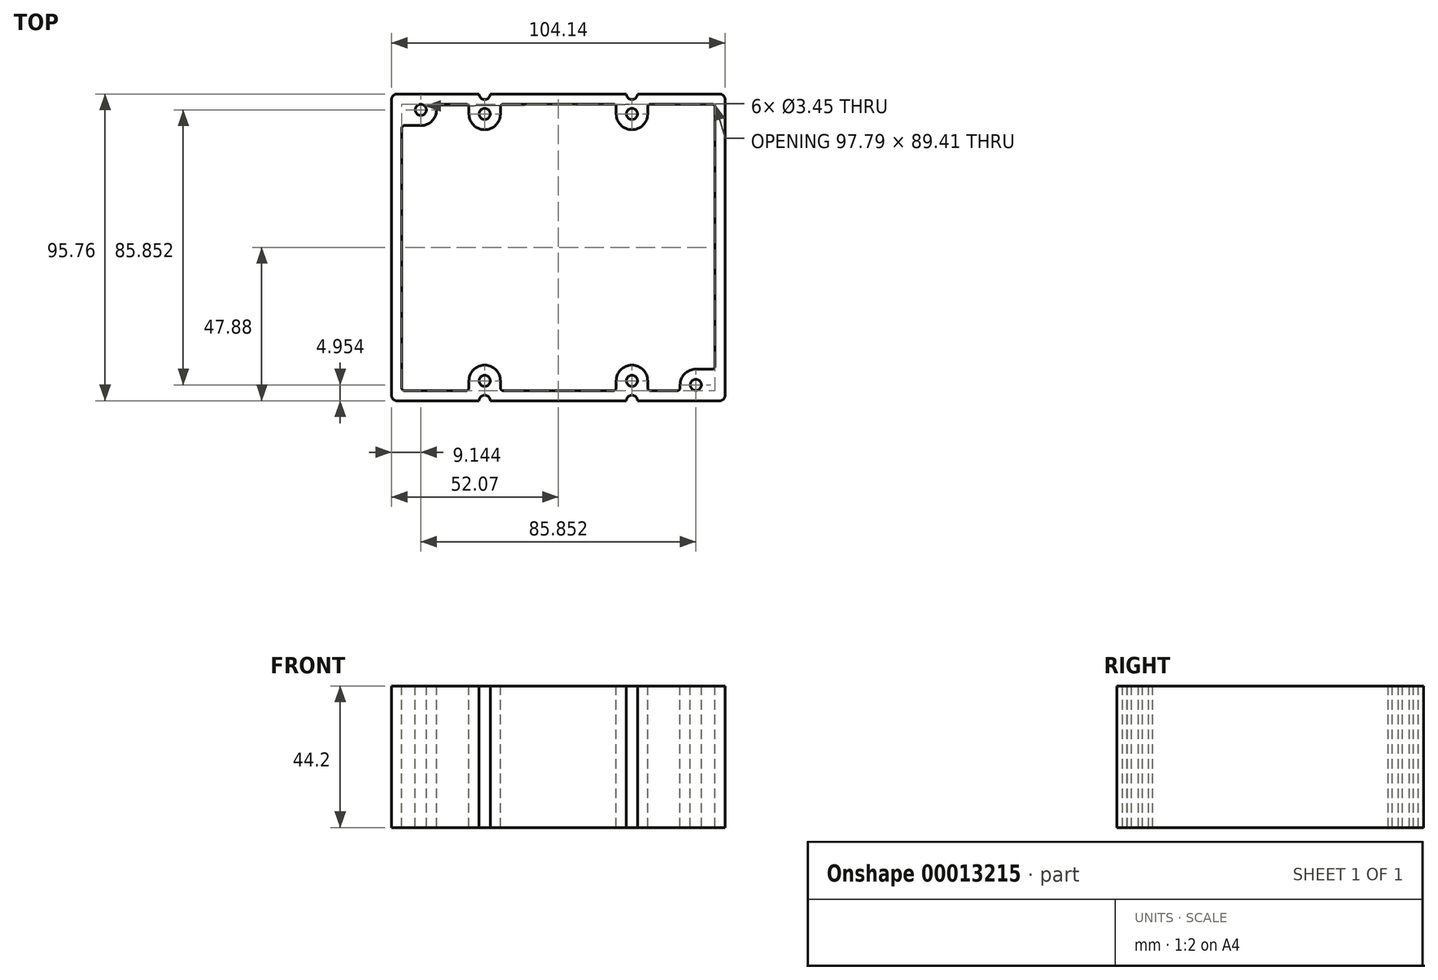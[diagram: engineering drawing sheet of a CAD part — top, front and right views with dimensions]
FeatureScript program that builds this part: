
annotation { "Feature Type Name" : "Feature", "Feature Type Description" : "" }
export const myFeature = defineFeature(function(context is Context, id is Id, definition is map)
    precondition{}
    {
        {
            var Q0;
            Q0=qCreatedBy(makeId("Front.planeOp"),FACE);
            var sketch = newSketch(context, id + "F0", { "sketchPlane" : qUnion([Q0])});
            skLineSegment(sketch, "E0.bottom", {"start": v(1.73, 0) * mm, "end": v(27.36, 0) * mm});
            skLineSegment(sketch, "E0.top", {"start": v(1.73, 95.76) * mm, "end": v(27.36, 95.76) * mm});
            skLineSegment(sketch, "E0.left", {"start": v(0, 1.73) * mm, "end": v(0, 94.03) * mm});
            skLineSegment(sketch, "E0.right", {"start": v(104.14, 1.73) * mm, "end": v(104.14, 94.03) * mm});
            skLineSegment(sketch, "E1", {"start": v(0, 47.88) * mm, "end": v(104.14, 47.88) * mm, "construction": true});
            skLineSegment(sketch, "E2", {"start": v(52.07, 95.76) * mm, "end": v(52.07, 0) * mm, "construction": true});
            skCircle(sketch, "E3", {"center": v(29.08, 89.53) * mm, "radius": 1.73 * mm});
            skCircle(sketch, "E4", {"center": v(29.08, 6.22) * mm, "radius": 1.73 * mm});
            skCircle(sketch, "E5", {"center": v(75.06, 89.53) * mm, "radius": 1.73 * mm});
            skCircle(sketch, "E6", {"center": v(75.06, 6.22) * mm, "radius": 1.73 * mm});
            skLineSegment(sketch, "E7", {"start": v(29.08, 89.53) * mm, "end": v(29.08, 6.22) * mm, "construction": true});
            skLineSegment(sketch, "E8", {"start": v(75.06, 6.22) * mm, "end": v(75.06, 89.53) * mm, "construction": true});
            skLineSegment(sketch, "E9", {"start": v(29.08, 89.53) * mm, "end": v(75.06, 89.53) * mm, "construction": true});
            skLineSegment(sketch, "E10", {"start": v(75.06, 6.22) * mm, "end": v(29.08, 6.22) * mm, "construction": true});
            skCircle(sketch, "E11", {"center": v(9.14, 4.95) * mm, "radius": 1.73 * mm});
            skCircle(sketch, "E12", {"center": v(95, 90.8) * mm, "radius": 1.73 * mm});
            skLineSegment(sketch, "E13.bottom", {"start": v(9.14, 4.95) * mm, "end": v(95, 4.95) * mm, "construction": true});
            skLineSegment(sketch, "E13.top", {"start": v(9.14, 90.8) * mm, "end": v(95, 90.8) * mm, "construction": true});
            skLineSegment(sketch, "E13.left", {"start": v(9.14, 4.95) * mm, "end": v(9.14, 90.8) * mm, "construction": true});
            skLineSegment(sketch, "E13.right", {"start": v(95, 4.95) * mm, "end": v(95, 90.8) * mm, "construction": true});
            skArc(sketch, "E14", {"start": v(27.36, 95.76) * mm, "mid": v(29.08, 94.03) * mm, "end": v(30.81, 95.76) * mm});
            skArc(sketch, "E15.0.MirrorCS", {"start": v(76.78, 95.76) * mm, "mid": v(75.06, 94.03) * mm, "end": v(73.33, 95.76) * mm});
            skArc(sketch, "E16.0.MirrorCS", {"start": v(27.36, 0) * mm, "mid": v(29.08, 1.73) * mm, "end": v(30.81, 0) * mm});
            skArc(sketch, "E17.0.MirrorCS", {"start": v(76.78, 0) * mm, "mid": v(75.06, 1.73) * mm, "end": v(73.33, 0) * mm});
            skPoint(sketch, "E18.visualSharp", {"position": v(0, 95.76) * mm});
            skArc(sketch, "E18.filletArc", {"start": v(1.73, 95.76) * mm, "mid": v(0.5, 95.25) * mm, "end": v(0, 94.03) * mm});
            skPoint(sketch, "E19.visualSharp", {"position": v(0, 0) * mm});
            skArc(sketch, "E19.filletArc", {"start": v(0, 1.73) * mm, "mid": v(0.5, 0.5) * mm, "end": v(1.73, 0) * mm});
            skPoint(sketch, "E20.visualSharp", {"position": v(104.14, 0) * mm});
            skArc(sketch, "E20.filletArc", {"start": v(102.41, 0) * mm, "mid": v(103.63, 0.5) * mm, "end": v(104.14, 1.73) * mm});
            skPoint(sketch, "E21.visualSharp", {"position": v(104.14, 95.76) * mm});
            skArc(sketch, "E21.filletArc", {"start": v(104.14, 94.03) * mm, "mid": v(103.63, 95.25) * mm, "end": v(102.41, 95.76) * mm});
            skLineSegment(sketch, "E22.trimOffspring", {"start": v(30.81, 95.76) * mm, "end": v(73.33, 95.76) * mm});
            skLineSegment(sketch, "E23.trimOffspring", {"start": v(76.78, 95.76) * mm, "end": v(102.41, 95.76) * mm});
            skLineSegment(sketch, "E24.trimOffspring", {"start": v(30.81, 0) * mm, "end": v(73.33, 0) * mm});
            skLineSegment(sketch, "E25.trimOffspring", {"start": v(76.78, 0) * mm, "end": v(102.41, 0) * mm});
            skLineSegment(sketch, "E26.0", {"start": v(80.82, 3.18) * mm, "end": v(100.1, 3.18) * mm});
            skLineSegment(sketch, "E26.5", {"start": v(100.97, 4.04) * mm, "end": v(100.97, 85.04) * mm});
            skLineSegment(sketch, "E26.6", {"start": v(3.17, 10.72) * mm, "end": v(3.17, 91.72) * mm});
            skLineSegment(sketch, "E26.7", {"start": v(4.04, 92.58) * mm, "end": v(23.32, 92.58) * mm});
            skLineSegment(sketch, "E26.9", {"start": v(34.85, 92.58) * mm, "end": v(69.3, 92.58) * mm});
            skLineSegment(sketch, "E26.11", {"start": v(80.82, 92.58) * mm, "end": v(89.23, 92.58) * mm});
            skArc(sketch, "E27.0", {"start": v(24.18, 89.53) * mm, "mid": v(29.08, 84.63) * mm, "end": v(33.99, 89.53) * mm});
            skArc(sketch, "E28.0", {"start": v(70.15, 89.53) * mm, "mid": v(75.06, 84.63) * mm, "end": v(79.96, 89.53) * mm});
            skLineSegment(sketch, "E29.0", {"start": v(71.22, 3.18) * mm, "end": v(71.22, 3.18) * mm});
            skArc(sketch, "E30.0", {"start": v(90.1, 90.8) * mm, "mid": v(91.53, 87.34) * mm, "end": v(95, 85.9) * mm});
            skArc(sketch, "E31.0", {"start": v(33.99, 6.22) * mm, "mid": v(29.08, 11.13) * mm, "end": v(24.18, 6.22) * mm});
            skArc(sketch, "E32.0", {"start": v(14.05, 4.95) * mm, "mid": v(12.61, 8.42) * mm, "end": v(9.14, 9.86) * mm});
            skLineSegment(sketch, "E33", {"start": v(95, 85.9) * mm, "end": v(100.1, 85.9) * mm});
            skLineSegment(sketch, "E34", {"start": v(90.1, 90.8) * mm, "end": v(90.1, 91.72) * mm});
            skLineSegment(sketch, "E35", {"start": v(79.96, 89.53) * mm, "end": v(79.96, 91.72) * mm});
            skLineSegment(sketch, "E36", {"start": v(70.15, 89.53) * mm, "end": v(70.15, 91.72) * mm});
            skLineSegment(sketch, "E37", {"start": v(33.99, 89.53) * mm, "end": v(33.99, 91.72) * mm});
            skLineSegment(sketch, "E38", {"start": v(24.18, 89.53) * mm, "end": v(24.18, 91.72) * mm});
            skLineSegment(sketch, "E39", {"start": v(9.14, 9.86) * mm, "end": v(4.04, 9.86) * mm});
            skLineSegment(sketch, "E40", {"start": v(14.05, 4.95) * mm, "end": v(14.05, 4.04) * mm});
            skLineSegment(sketch, "E41", {"start": v(24.18, 6.22) * mm, "end": v(24.18, 4.04) * mm});
            skLineSegment(sketch, "E42", {"start": v(33.99, 6.22) * mm, "end": v(33.99, 4.04) * mm});
            skLineSegment(sketch, "E43", {"start": v(79.96, 6.22) * mm, "end": v(79.96, 4.04) * mm});
            skLineSegment(sketch, "E44", {"start": v(70.15, 6.22) * mm, "end": v(70.15, 4.04) * mm});
            skArc(sketch, "E45.trimOffspring", {"start": v(79.96, 6.22) * mm, "mid": v(75.06, 11.13) * mm, "end": v(70.15, 6.22) * mm});
            skLineSegment(sketch, "E46.trimOffspring", {"start": v(34.85, 3.18) * mm, "end": v(69.3, 3.18) * mm});
            skLineSegment(sketch, "E47.trimOffspring", {"start": v(14.9, 3.18) * mm, "end": v(23.32, 3.18) * mm});
            skPoint(sketch, "E48.visualSharp", {"position": v(3.17, 92.58) * mm});
            skArc(sketch, "E48.filletArc", {"start": v(4.04, 92.58) * mm, "mid": v(3.43, 92.33) * mm, "end": v(3.18, 91.72) * mm});
            skPoint(sketch, "E49.visualSharp", {"position": v(24.18, 92.58) * mm});
            skArc(sketch, "E49.filletArc", {"start": v(24.18, 91.72) * mm, "mid": v(23.93, 92.33) * mm, "end": v(23.32, 92.58) * mm});
            skPoint(sketch, "E50.visualSharp", {"position": v(33.99, 92.58) * mm});
            skArc(sketch, "E50.filletArc", {"start": v(34.85, 92.58) * mm, "mid": v(34.24, 92.33) * mm, "end": v(33.99, 91.72) * mm});
            skPoint(sketch, "E51.visualSharp", {"position": v(70.15, 92.58) * mm});
            skArc(sketch, "E51.filletArc", {"start": v(70.15, 91.72) * mm, "mid": v(69.9, 92.33) * mm, "end": v(69.3, 92.58) * mm});
            skPoint(sketch, "E52.visualSharp", {"position": v(79.96, 92.58) * mm});
            skArc(sketch, "E52.filletArc", {"start": v(80.82, 92.58) * mm, "mid": v(80.21, 92.33) * mm, "end": v(79.96, 91.72) * mm});
            skPoint(sketch, "E53.visualSharp", {"position": v(90.1, 92.58) * mm});
            skArc(sketch, "E53.filletArc", {"start": v(90.1, 91.72) * mm, "mid": v(89.84, 92.33) * mm, "end": v(89.23, 92.58) * mm});
            skPoint(sketch, "E54.visualSharp", {"position": v(100.97, 85.9) * mm});
            skArc(sketch, "E54.filletArc", {"start": v(100.97, 85.04) * mm, "mid": v(100.71, 85.65) * mm, "end": v(100.1, 85.9) * mm});
            skPoint(sketch, "E55.visualSharp", {"position": v(100.97, 3.18) * mm});
            skArc(sketch, "E55.filletArc", {"start": v(100.1, 3.17) * mm, "mid": v(100.71, 3.43) * mm, "end": v(100.97, 4.04) * mm});
            skPoint(sketch, "E56.visualSharp", {"position": v(79.96, 3.18) * mm});
            skArc(sketch, "E56.filletArc", {"start": v(79.96, 4.04) * mm, "mid": v(80.21, 3.43) * mm, "end": v(80.82, 3.18) * mm});
            skPoint(sketch, "E57.visualSharp", {"position": v(70.15, 3.18) * mm});
            skArc(sketch, "E57.filletArc", {"start": v(69.3, 3.18) * mm, "mid": v(69.9, 3.43) * mm, "end": v(70.15, 4.04) * mm});
            skPoint(sketch, "E58.visualSharp", {"position": v(33.99, 3.18) * mm});
            skArc(sketch, "E58.filletArc", {"start": v(33.99, 4.04) * mm, "mid": v(34.24, 3.43) * mm, "end": v(34.85, 3.18) * mm});
            skPoint(sketch, "E59.visualSharp", {"position": v(24.18, 3.18) * mm});
            skArc(sketch, "E59.filletArc", {"start": v(23.32, 3.18) * mm, "mid": v(23.93, 3.43) * mm, "end": v(24.18, 4.04) * mm});
            skPoint(sketch, "E60.visualSharp", {"position": v(14.05, 3.18) * mm});
            skArc(sketch, "E60.filletArc", {"start": v(14.05, 4.04) * mm, "mid": v(14.3, 3.43) * mm, "end": v(14.9, 3.18) * mm});
            skPoint(sketch, "E61.visualSharp", {"position": v(3.17, 9.86) * mm});
            skArc(sketch, "E61.filletArc", {"start": v(3.17, 10.72) * mm, "mid": v(3.43, 10.1) * mm, "end": v(4.04, 9.86) * mm});
            skSolve(sketch);
        }
        {
            var Q0;
            Q0 = qSketchRegion(id + "F0", true);
            extrude(context, id + "F1", {"entities" : qUnion([Q0]), "depth" : 44.2 * mm});
        }
        {
            var Q0;
            Q0=makeQuery(id+"F1.opExtrude","SWEPT_BODY",BODY,{"disambiguationData":[OSD([sQuery(id+"F0.wireOp",EDGE,"E0.bottom"),sQuery(id+"F0.wireOp",EDGE,"E0.top"),sQuery(id+"F0.wireOp",EDGE,"E0.left"),sQuery(id+"F0.wireOp",EDGE,"E0.right"),sQuery(id+"F0.wireOp",EDGE,"E3"),sQuery(id+"F0.wireOp",EDGE,"E4"),sQuery(id+"F0.wireOp",EDGE,"E5"),sQuery(id+"F0.wireOp",EDGE,"E6"),sQuery(id+"F0.wireOp",EDGE,"E11"),sQuery(id+"F0.wireOp",EDGE,"E12"),sQuery(id+"F0.wireOp",EDGE,"E14"),sQuery(id+"F0.wireOp",EDGE,"E15.0.MirrorCS"),sQuery(id+"F0.wireOp",EDGE,"E16.0.MirrorCS"),sQuery(id+"F0.wireOp",EDGE,"E17.0.MirrorCS"),sQuery(id+"F0.wireOp",EDGE,"E18.filletArc"),sQuery(id+"F0.wireOp",EDGE,"E19.filletArc"),sQuery(id+"F0.wireOp",EDGE,"E20.filletArc"),sQuery(id+"F0.wireOp",EDGE,"E21.filletArc"),sQuery(id+"F0.wireOp",EDGE,"E22.trimOffspring"),sQuery(id+"F0.wireOp",EDGE,"E23.trimOffspring"),sQuery(id+"F0.wireOp",EDGE,"E24.trimOffspring"),sQuery(id+"F0.wireOp",EDGE,"E25.trimOffspring"),sQuery(id+"F0.wireOp",EDGE,"E26.0"),sQuery(id+"F0.wireOp",EDGE,"E26.5"),sQuery(id+"F0.wireOp",EDGE,"E26.6"),sQuery(id+"F0.wireOp",EDGE,"E26.7"),sQuery(id+"F0.wireOp",EDGE,"E26.9"),sQuery(id+"F0.wireOp",EDGE,"E26.11"),sQuery(id+"F0.wireOp",EDGE,"E27.0"),sQuery(id+"F0.wireOp",EDGE,"E28.0"),sQuery(id+"F0.wireOp",EDGE,"E30.0"),sQuery(id+"F0.wireOp",EDGE,"E31.0"),sQuery(id+"F0.wireOp",EDGE,"E32.0"),sQuery(id+"F0.wireOp",EDGE,"E33"),sQuery(id+"F0.wireOp",EDGE,"E34"),sQuery(id+"F0.wireOp",EDGE,"E35"),sQuery(id+"F0.wireOp",EDGE,"E36"),sQuery(id+"F0.wireOp",EDGE,"E37"),sQuery(id+"F0.wireOp",EDGE,"E38"),sQuery(id+"F0.wireOp",EDGE,"E39"),sQuery(id+"F0.wireOp",EDGE,"E40"),sQuery(id+"F0.wireOp",EDGE,"E41"),sQuery(id+"F0.wireOp",EDGE,"E42"),sQuery(id+"F0.wireOp",EDGE,"E43"),sQuery(id+"F0.wireOp",EDGE,"E44"),sQuery(id+"F0.wireOp",EDGE,"E45.trimOffspring"),sQuery(id+"F0.wireOp",EDGE,"E46.trimOffspring"),sQuery(id+"F0.wireOp",EDGE,"E47.trimOffspring"),sQuery(id+"F0.wireOp",EDGE,"E48.filletArc"),sQuery(id+"F0.wireOp",EDGE,"E49.filletArc"),sQuery(id+"F0.wireOp",EDGE,"E50.filletArc"),sQuery(id+"F0.wireOp",EDGE,"E51.filletArc"),sQuery(id+"F0.wireOp",EDGE,"E52.filletArc"),sQuery(id+"F0.wireOp",EDGE,"E53.filletArc"),sQuery(id+"F0.wireOp",EDGE,"E54.filletArc"),sQuery(id+"F0.wireOp",EDGE,"E55.filletArc"),sQuery(id+"F0.wireOp",EDGE,"E56.filletArc"),sQuery(id+"F0.wireOp",EDGE,"E57.filletArc"),sQuery(id+"F0.wireOp",EDGE,"E58.filletArc"),sQuery(id+"F0.wireOp",EDGE,"E59.filletArc"),sQuery(id+"F0.wireOp",EDGE,"E60.filletArc"),sQuery(id+"F0.wireOp",EDGE,"E61.filletArc")])]});
            transform(context, id + "F2", {"entities" : qUnion([Q0]), "transformType" : TransformType.TRANSLATION_3D, "dx" : -52.07 * mm, "dy" : 44.2 * mm, "dz" : -47.88 * mm, "makeCopy" : false});
        }
        {
            var Q0;
            Q0=qCreatedBy(makeId("Front.planeOp"),FACE);
            var sketch = newSketch(context, id + "F3", { "sketchPlane" : qUnion([Q0])});
            skLineSegment(sketch, "E62", {"start": v(-48.55, 0) * mm, "end": v(0, 0) * mm});
            skSolve(sketch);
        }
        {
            var Q0;
            Q0=makeQuery(id+"F1.opExtrude","SWEPT_BODY",BODY,{"disambiguationData":[OSD([sQuery(id+"F0.wireOp",EDGE,"E0.bottom"),sQuery(id+"F0.wireOp",EDGE,"E0.top"),sQuery(id+"F0.wireOp",EDGE,"E0.left"),sQuery(id+"F0.wireOp",EDGE,"E0.right"),sQuery(id+"F0.wireOp",EDGE,"E3"),sQuery(id+"F0.wireOp",EDGE,"E4"),sQuery(id+"F0.wireOp",EDGE,"E5"),sQuery(id+"F0.wireOp",EDGE,"E6"),sQuery(id+"F0.wireOp",EDGE,"E11"),sQuery(id+"F0.wireOp",EDGE,"E12"),sQuery(id+"F0.wireOp",EDGE,"E14"),sQuery(id+"F0.wireOp",EDGE,"E15.0.MirrorCS"),sQuery(id+"F0.wireOp",EDGE,"E16.0.MirrorCS"),sQuery(id+"F0.wireOp",EDGE,"E17.0.MirrorCS"),sQuery(id+"F0.wireOp",EDGE,"E18.filletArc"),sQuery(id+"F0.wireOp",EDGE,"E19.filletArc"),sQuery(id+"F0.wireOp",EDGE,"E20.filletArc"),sQuery(id+"F0.wireOp",EDGE,"E21.filletArc"),sQuery(id+"F0.wireOp",EDGE,"E22.trimOffspring"),sQuery(id+"F0.wireOp",EDGE,"E23.trimOffspring"),sQuery(id+"F0.wireOp",EDGE,"E24.trimOffspring"),sQuery(id+"F0.wireOp",EDGE,"E25.trimOffspring"),sQuery(id+"F0.wireOp",EDGE,"E26.0"),sQuery(id+"F0.wireOp",EDGE,"E26.5"),sQuery(id+"F0.wireOp",EDGE,"E26.6"),sQuery(id+"F0.wireOp",EDGE,"E26.7"),sQuery(id+"F0.wireOp",EDGE,"E26.9"),sQuery(id+"F0.wireOp",EDGE,"E26.11"),sQuery(id+"F0.wireOp",EDGE,"E27.0"),sQuery(id+"F0.wireOp",EDGE,"E28.0"),sQuery(id+"F0.wireOp",EDGE,"E30.0"),sQuery(id+"F0.wireOp",EDGE,"E31.0"),sQuery(id+"F0.wireOp",EDGE,"E32.0"),sQuery(id+"F0.wireOp",EDGE,"E33"),sQuery(id+"F0.wireOp",EDGE,"E34"),sQuery(id+"F0.wireOp",EDGE,"E35"),sQuery(id+"F0.wireOp",EDGE,"E36"),sQuery(id+"F0.wireOp",EDGE,"E37"),sQuery(id+"F0.wireOp",EDGE,"E38"),sQuery(id+"F0.wireOp",EDGE,"E39"),sQuery(id+"F0.wireOp",EDGE,"E40"),sQuery(id+"F0.wireOp",EDGE,"E41"),sQuery(id+"F0.wireOp",EDGE,"E42"),sQuery(id+"F0.wireOp",EDGE,"E43"),sQuery(id+"F0.wireOp",EDGE,"E44"),sQuery(id+"F0.wireOp",EDGE,"E45.trimOffspring"),sQuery(id+"F0.wireOp",EDGE,"E46.trimOffspring"),sQuery(id+"F0.wireOp",EDGE,"E47.trimOffspring"),sQuery(id+"F0.wireOp",EDGE,"E48.filletArc"),sQuery(id+"F0.wireOp",EDGE,"E49.filletArc"),sQuery(id+"F0.wireOp",EDGE,"E50.filletArc"),sQuery(id+"F0.wireOp",EDGE,"E51.filletArc"),sQuery(id+"F0.wireOp",EDGE,"E52.filletArc"),sQuery(id+"F0.wireOp",EDGE,"E53.filletArc"),sQuery(id+"F0.wireOp",EDGE,"E54.filletArc"),sQuery(id+"F0.wireOp",EDGE,"E55.filletArc"),sQuery(id+"F0.wireOp",EDGE,"E56.filletArc"),sQuery(id+"F0.wireOp",EDGE,"E57.filletArc"),sQuery(id+"F0.wireOp",EDGE,"E58.filletArc"),sQuery(id+"F0.wireOp",EDGE,"E59.filletArc"),sQuery(id+"F0.wireOp",EDGE,"E60.filletArc"),sQuery(id+"F0.wireOp",EDGE,"E61.filletArc")])]});
            var Q1;
            Q1=sQuery(id+"F3.wireOp",EDGE,"E62");
            transform(context, id + "F4", {"entities" : qUnion([Q0]), "transformType" : TransformType.ROTATION, "transformAxis" : qUnion([Q1]), "angle" : 90 * degree, "makeCopy" : false});
        }
        {
            var Q0;
            Q0=makeQuery(id+"F1.opExtrude","SWEPT_BODY",BODY,{"disambiguationData":[OSD([sQuery(id+"F0.wireOp",EDGE,"E0.bottom"),sQuery(id+"F0.wireOp",EDGE,"E0.top"),sQuery(id+"F0.wireOp",EDGE,"E0.left"),sQuery(id+"F0.wireOp",EDGE,"E0.right"),sQuery(id+"F0.wireOp",EDGE,"E3"),sQuery(id+"F0.wireOp",EDGE,"E4"),sQuery(id+"F0.wireOp",EDGE,"E5"),sQuery(id+"F0.wireOp",EDGE,"E6"),sQuery(id+"F0.wireOp",EDGE,"E11"),sQuery(id+"F0.wireOp",EDGE,"E12"),sQuery(id+"F0.wireOp",EDGE,"E14"),sQuery(id+"F0.wireOp",EDGE,"E15.0.MirrorCS"),sQuery(id+"F0.wireOp",EDGE,"E16.0.MirrorCS"),sQuery(id+"F0.wireOp",EDGE,"E17.0.MirrorCS"),sQuery(id+"F0.wireOp",EDGE,"E18.filletArc"),sQuery(id+"F0.wireOp",EDGE,"E19.filletArc"),sQuery(id+"F0.wireOp",EDGE,"E20.filletArc"),sQuery(id+"F0.wireOp",EDGE,"E21.filletArc"),sQuery(id+"F0.wireOp",EDGE,"E22.trimOffspring"),sQuery(id+"F0.wireOp",EDGE,"E23.trimOffspring"),sQuery(id+"F0.wireOp",EDGE,"E24.trimOffspring"),sQuery(id+"F0.wireOp",EDGE,"E25.trimOffspring"),sQuery(id+"F0.wireOp",EDGE,"E26.0"),sQuery(id+"F0.wireOp",EDGE,"E26.5"),sQuery(id+"F0.wireOp",EDGE,"E26.6"),sQuery(id+"F0.wireOp",EDGE,"E26.7"),sQuery(id+"F0.wireOp",EDGE,"E26.9"),sQuery(id+"F0.wireOp",EDGE,"E26.11"),sQuery(id+"F0.wireOp",EDGE,"E27.0"),sQuery(id+"F0.wireOp",EDGE,"E28.0"),sQuery(id+"F0.wireOp",EDGE,"E30.0"),sQuery(id+"F0.wireOp",EDGE,"E31.0"),sQuery(id+"F0.wireOp",EDGE,"E32.0"),sQuery(id+"F0.wireOp",EDGE,"E33"),sQuery(id+"F0.wireOp",EDGE,"E34"),sQuery(id+"F0.wireOp",EDGE,"E35"),sQuery(id+"F0.wireOp",EDGE,"E36"),sQuery(id+"F0.wireOp",EDGE,"E37"),sQuery(id+"F0.wireOp",EDGE,"E38"),sQuery(id+"F0.wireOp",EDGE,"E39"),sQuery(id+"F0.wireOp",EDGE,"E40"),sQuery(id+"F0.wireOp",EDGE,"E41"),sQuery(id+"F0.wireOp",EDGE,"E42"),sQuery(id+"F0.wireOp",EDGE,"E43"),sQuery(id+"F0.wireOp",EDGE,"E44"),sQuery(id+"F0.wireOp",EDGE,"E45.trimOffspring"),sQuery(id+"F0.wireOp",EDGE,"E46.trimOffspring"),sQuery(id+"F0.wireOp",EDGE,"E47.trimOffspring"),sQuery(id+"F0.wireOp",EDGE,"E48.filletArc"),sQuery(id+"F0.wireOp",EDGE,"E49.filletArc"),sQuery(id+"F0.wireOp",EDGE,"E50.filletArc"),sQuery(id+"F0.wireOp",EDGE,"E51.filletArc"),sQuery(id+"F0.wireOp",EDGE,"E52.filletArc"),sQuery(id+"F0.wireOp",EDGE,"E53.filletArc"),sQuery(id+"F0.wireOp",EDGE,"E54.filletArc"),sQuery(id+"F0.wireOp",EDGE,"E55.filletArc"),sQuery(id+"F0.wireOp",EDGE,"E56.filletArc"),sQuery(id+"F0.wireOp",EDGE,"E57.filletArc"),sQuery(id+"F0.wireOp",EDGE,"E58.filletArc"),sQuery(id+"F0.wireOp",EDGE,"E59.filletArc"),sQuery(id+"F0.wireOp",EDGE,"E60.filletArc"),sQuery(id+"F0.wireOp",EDGE,"E61.filletArc")])]});
            transform(context, id + "F5", {"entities" : qUnion([Q0]), "transformType" : TransformType.TRANSLATION_3D, "dx" : 0 * mm, "dy" : 0 * mm, "dz" : -44.2 * mm, "makeCopy" : false});
        }
    });
